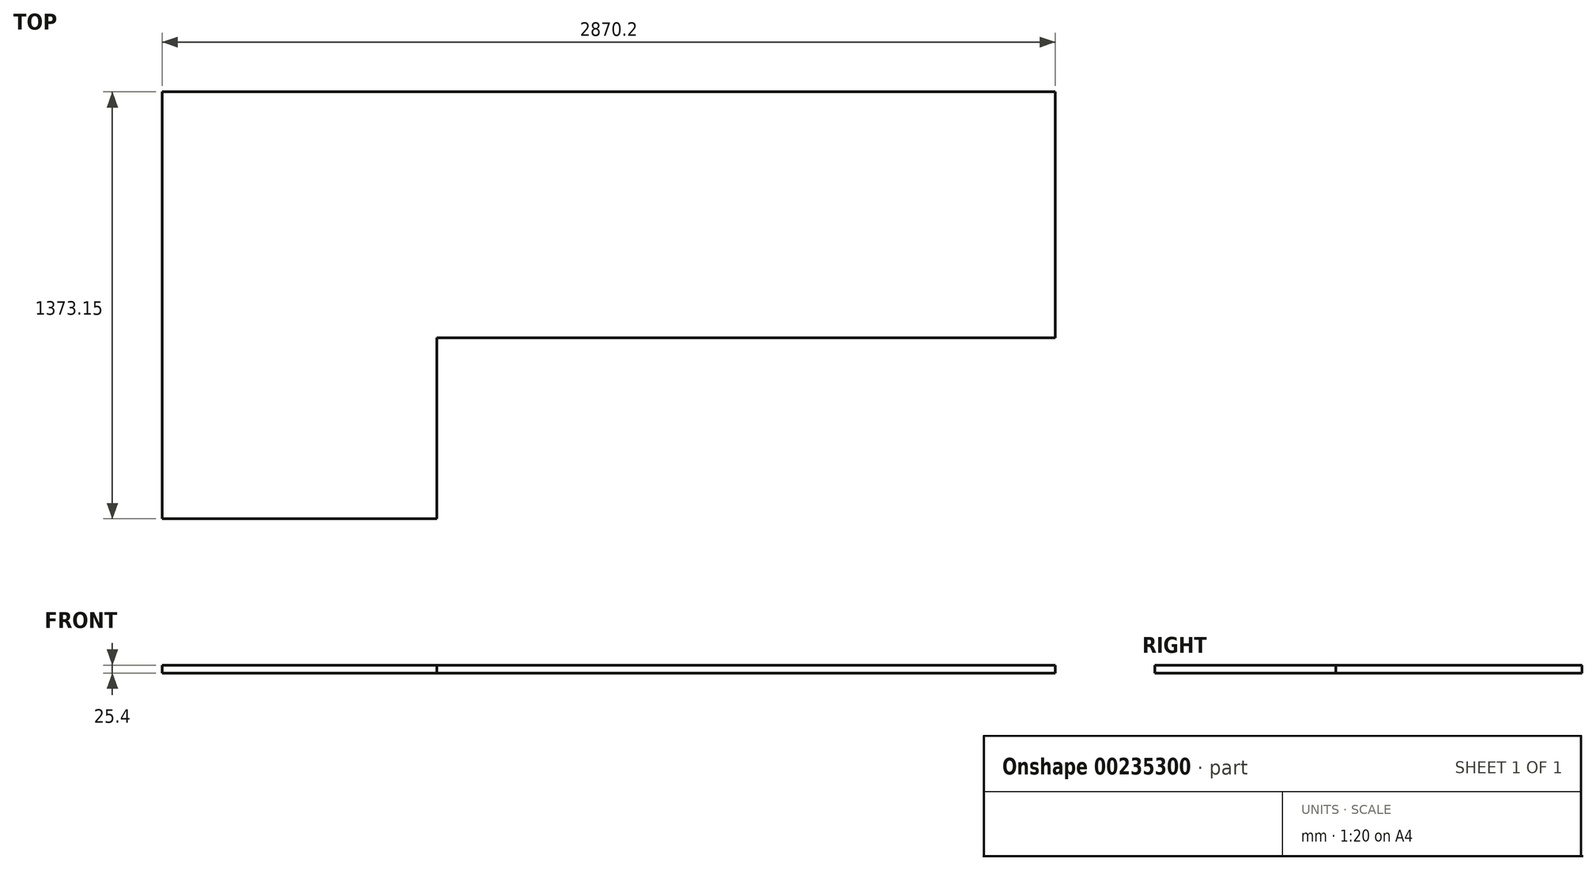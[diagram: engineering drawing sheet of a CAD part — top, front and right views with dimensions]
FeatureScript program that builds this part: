
annotation { "Feature Type Name" : "Feature", "Feature Type Description" : "" }
export const myFeature = defineFeature(function(context is Context, id is Id, definition is map)
    precondition{}
    {
        {
            var Q0;
            Q0=qCreatedBy(makeId("Top.planeOp"),FACE);
            var sketch = newSketch(context, id + "F0", { "sketchPlane" : qUnion([Q0])});
            skLineSegment(sketch, "E0", {"start": v(-1436.74, 658.27) * mm, "end": v(-1436.74, -714.88) * mm});
            skLineSegment(sketch, "E1", {"start": v(-1436.74, -714.88) * mm, "end": v(-553.6, -714.88) * mm});
            skLineSegment(sketch, "E2", {"start": v(-553.6, -714.88) * mm, "end": v(-553.6, -132.7) * mm});
            skLineSegment(sketch, "E3", {"start": v(-553.6, -132.7) * mm, "end": v(1433.46, -132.7) * mm});
            skLineSegment(sketch, "E4", {"start": v(1433.46, -132.7) * mm, "end": v(1433.46, 658.27) * mm});
            skLineSegment(sketch, "E5", {"start": v(1433.46, 658.27) * mm, "end": v(-1436.74, 658.27) * mm});
            skSolve(sketch);
        }
        {
            var Q0;
            Q0=makeQuery(id+"F0.imprint","IMPRINT",FACE,{"disambiguationData":[TD([[makeQuery(id+"F0.imprint","IMPRINT",EDGE,{"derivedFrom":sQuery(id+"F0.wireOp",EDGE,"E0")}),1.0]])]});
            extrude(context, id + "F1", {"entities" : qUnion([Q0]), "depth" : 25.4 * mm});
        }
    });
